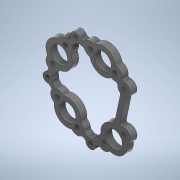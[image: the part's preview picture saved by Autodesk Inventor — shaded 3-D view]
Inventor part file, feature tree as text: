
AUTODESK INVENTOR PART (.ipt)
format: ipt  version: 2020.2 (Build 242310000, 310)  size: 621,056 bytes
history: native  units: mm
features: other x3, extrude x3, sketch x3, fillet x2
ambient origin geometry x8: Origin, YZ Plane, XZ Plane, XY Plane, X Axis, Y Axis, Z Axis, Center Point
bodies: Body1 (feature_tree)
feature tree (11):
  other  "ソリッド1"
  extrude  "押し出し1"  Depth=3.0mm
  fillet  "フィレット1"  Radius=3.0mm
  extrude  "押し出し2"  Depth=3.0mm
  extrude  "押し出し3"  Depth=4.0mm TaperAngle=0.0deg
  fillet  "フィレット2"  Radius=1.0mm
  sketch  "スケッチ1"
  sketch  "スケッチ2"
  sketch  "スケッチ3"
  other  "断面エッジを投影1"
  other  "断面エッジを投影2"
